# Revit family: NAU_Naughtone_Stng_Penny_AFTERQA
name_source: partatom
category: Furniture
units: mm (PartAtom-declared; Revit-internal decimal feet)

## family parameters
Always vertical = Yes
Cut with Voids When Loaded = No
OmniClass Number = 23.40.20.00
OmniClass Title = General Furniture and Specialties
Room Calculation Point = No
Shared = No
Work Plane-Based = No

## types (3) — shared parameters
Assembly Code = E2020
AssetType = Movable
BIMObjectName = NAU_Naughtone_Seating_Penny
Category = Pr_40_50_12 : Chairs, seats and benches
Color = Black base. Oak seat
DurationUnit = year
Features = Legs available in 16 different RALs. Tops available in solid oak or walnut
Finish = Base is powdercoated steel in RAL 9005 black
FootMaterial = NAU_Generic_Plastic_Black
FrameMaterial = NAU_Generic_Metal_Steel_PowderCoatedSteelRAL9005Black
IfcExportAs = IfcFurnishingElementType
IfcExportType = CHAIR
ManufacturerName = Naughtone
ManufacturerURL = www.naughtone.com
Material = Legs in steel. Seat top in solid wood
NBSDescription = Seating
NBSReference = 45-35-72/352
Name = Seating_Penny_Naughtone
ProductInformation = www.naughtone.com
SeatDiameter = 160 mm  [stored 0.524934 ft]
SeatMaterial = NAU_Generic_Wood_Oak
Shape = Circular
URL = www.naughtone.com
Uniclass2015Code = Pr_40_50_12
Uniclass2015Title = Chairs, seats and benches
Uniclass2015Version = Products v1.26
Version = 1
WarrantyDescription = Request warranty information from naughtone
WarrantyDurationLabor = 10
WarrantyDurationParts = 10
WarrantyDurationUnit = year
zero-valued in all types: Default Elevation, NumberOfChairs, WorksurfaceArea

## per-type parameters (varying)
| type | IsMedium | IsSmall | IsTall | ModelNumber | NominalHeight | NominalLength | NominalWidth | Size |
| Penny Low Stool | No | Yes | No | NOPENLO | 450 mm  [stored 1.47638 ft] | 350 mm  [stored 1.14829 ft] | 350 mm  [stored 1.14829 ft] | 350 x 350 x 450 mm |
| Penny Counter Height Stool | Yes | No | No | NOPENCH | 650 mm  [stored 2.13255 ft] | 425 mm  [stored 1.39436 ft] | 425 mm  [stored 1.39436 ft] | 425 x 425 x 650mm |
| Penny Bar Stool | No | No | Yes | NOPENBS | 750 mm  [stored 2.46063 ft] | 425 mm  [stored 1.39436 ft] | 425 mm  [stored 1.39436 ft] | 425 x 425 x 750mm |

note: column(s) folded — value = type name in every type: ModelReference

note: [stored X ft] marks values corroborated as IEEE doubles in the binary element streams (Revit-internal decimal feet)

## geometry (parser evidence)
native form markers: Sweep x6
no freeform markers — native parametric forms only
